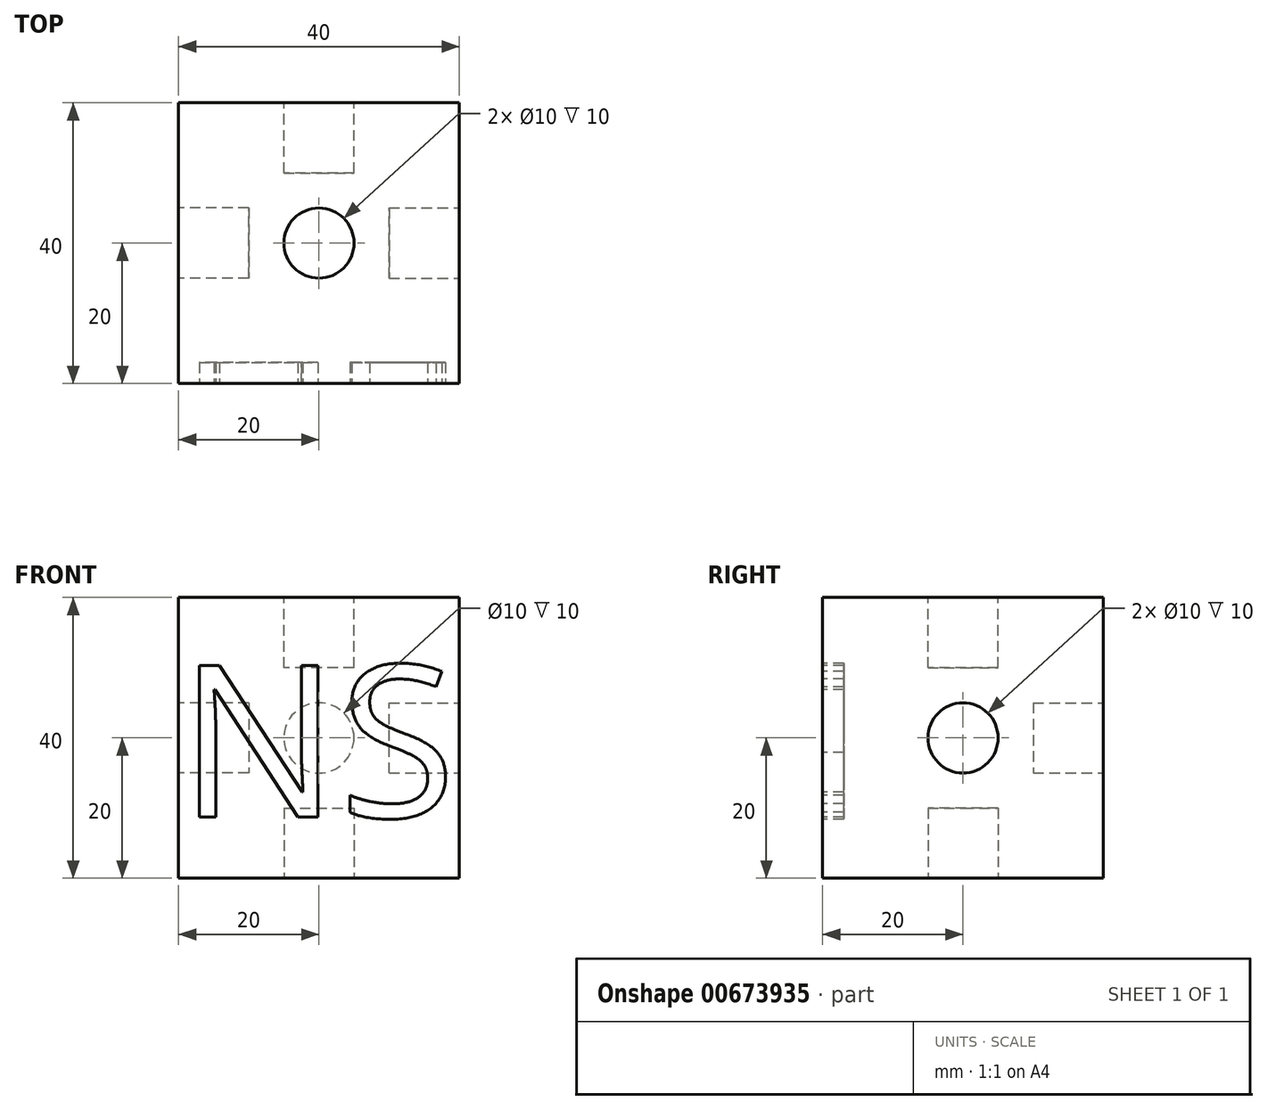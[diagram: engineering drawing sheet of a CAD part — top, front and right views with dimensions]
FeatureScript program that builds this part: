
annotation { "Feature Type Name" : "Feature", "Feature Type Description" : "" }
export const myFeature = defineFeature(function(context is Context, id is Id, definition is map)
    precondition{}
    {
        {
            var Q0;
            Q0=qCreatedBy(makeId("Front.planeOp"),FACE);
            var sketch = newSketch(context, id + "F0", { "sketchPlane" : qUnion([Q0])});
            skLineSegment(sketch, "E0.bottom", {"start": v(0, 0) * mm, "end": v(40, 0) * mm});
            skLineSegment(sketch, "E0.top", {"start": v(0, 40) * mm, "end": v(40, 40) * mm});
            skLineSegment(sketch, "E0.left", {"start": v(0, 0) * mm, "end": v(0, 40) * mm});
            skLineSegment(sketch, "E0.right", {"start": v(40, 0) * mm, "end": v(40, 40) * mm});
            skSolve(sketch);
        }
        {
            var Q0;
            Q0 = qSketchRegion(id + "F0", true);
            extrude(context, id + "F1", {"entities" : qUnion([Q0]), "depth" : 40 * mm, "offsetDistance" : 25 * mm});
        }
        {
            var Q0;
            Q0=makeQuery(id+"F1.opExtrude","SWEPT_FACE",FACE,{"disambiguationData":[OSD([sQuery(id+"F0.wireOp",EDGE,"E0.left")])]});
            var sketch = newSketch(context, id + "F2", { "sketchPlane" : qUnion([Q0])});
            skCircle(sketch, "E1", {"center": v(20, 20) * mm, "radius": 5 * mm});
            skPoint(sketch, "E1.centerSnap0", {"position": v(20, 40) * mm});
            skPoint(sketch, "E1.centerSnap1", {"position": v(0, 20) * mm});
            skSolve(sketch);
        }
        {
            var Q0;
            Q0 = qSketchRegion(id + "F2", true);
            extrude(context, id + "F3", {"entities" : qUnion([Q0]), "operationType" : NewBodyOperationType.REMOVE, "depth" : -10 * mm, "offsetDistance" : 25 * mm});
        }
        {
            var Q0;
            Q0=makeQuery(id+"F1.opExtrude","SWEPT_FACE",FACE,{"disambiguationData":[OSD([sQuery(id+"F0.wireOp",EDGE,"E0.right")])]});
            var sketch = newSketch(context, id + "F4", { "sketchPlane" : qUnion([Q0])});
            skCircle(sketch, "E2", {"center": v(-20, 20) * mm, "radius": 5 * mm});
            skPoint(sketch, "E2.centerSnap0", {"position": v(0, 20) * mm});
            skPoint(sketch, "E2.centerSnap1", {"position": v(-20, 0) * mm});
            skSolve(sketch);
        }
        {
            var Q0;
            Q0 = qSketchRegion(id + "F4", true);
            extrude(context, id + "F5", {"entities" : qUnion([Q0]), "operationType" : NewBodyOperationType.REMOVE, "depth" : -10 * mm, "offsetDistance" : 25 * mm});
        }
        {
            var Q0;
            Q0=makeQuery(id+"F1.opExtrude","CAP_FACE",FACE,{"disambiguationData":[OSD([sQuery(id+"F0.wireOp",EDGE,"E0.bottom"),sQuery(id+"F0.wireOp",EDGE,"E0.top"),sQuery(id+"F0.wireOp",EDGE,"E0.left"),sQuery(id+"F0.wireOp",EDGE,"E0.right")])],"isStart":false});
            var sketch = newSketch(context, id + "F6", { "sketchPlane" : qUnion([Q0])});
            skText(sketch, "E3", { "text": "NS", "fontName": "OpenSans-Regular.ttf"});
            const initialGuessF6  = {"E3": [0, 0.0087, 1, 0, 0.02182]};
            skSetInitialGuess(sketch, initialGuessF6);
            skSolve(sketch);
        }
        {
            var Q0;
            Q0 = qSketchRegion(id + "F6", true);
            extrude(context, id + "F7", {"entities" : qUnion([Q0]), "operationType" : NewBodyOperationType.REMOVE, "oppositeDirection" : true, "depth" : 3 * mm, "offsetDistance" : 25 * mm});
        }
        {
            var Q0;
            Q0=makeQuery(id+"F1.opExtrude","SWEPT_FACE",FACE,{"disambiguationData":[OSD([sQuery(id+"F0.wireOp",EDGE,"E0.top")])]});
            var sketch = newSketch(context, id + "F8", { "sketchPlane" : qUnion([Q0])});
            skCircle(sketch, "E4", {"center": v(20, -20) * mm, "radius": 5 * mm});
            skPoint(sketch, "E4.centerSnap0", {"position": v(20, 0) * mm});
            skPoint(sketch, "E4.centerSnap1", {"position": v(0, -20) * mm});
            skSolve(sketch);
        }
        {
            var Q0;
            Q0 = qSketchRegion(id + "F8", true);
            extrude(context, id + "F9", {"entities" : qUnion([Q0]), "operationType" : NewBodyOperationType.REMOVE, "oppositeDirection" : true, "depth" : 10 * mm, "offsetDistance" : 25 * mm});
        }
        {
            var Q0;
            Q0=makeQuery(id+"F1.opExtrude","SWEPT_FACE",FACE,{"disambiguationData":[OSD([sQuery(id+"F0.wireOp",EDGE,"E0.bottom")])]});
            var sketch = newSketch(context, id + "F10", { "sketchPlane" : qUnion([Q0])});
            skCircle(sketch, "E5", {"center": v(20, 20) * mm, "radius": 5 * mm});
            skPoint(sketch, "E5.centerSnap0", {"position": v(20, 40) * mm});
            skPoint(sketch, "E5.centerSnap1", {"position": v(0, 20) * mm});
            skSolve(sketch);
        }
        {
            var Q0;
            Q0 = qSketchRegion(id + "F10", true);
            extrude(context, id + "F11", {"entities" : qUnion([Q0]), "operationType" : NewBodyOperationType.REMOVE, "oppositeDirection" : true, "depth" : 10 * mm, "offsetDistance" : 25 * mm});
        }
        {
            var Q0;
            Q0=makeQuery(id+"F1.opExtrude","CAP_FACE",FACE,{"disambiguationData":[OSD([sQuery(id+"F0.wireOp",EDGE,"E0.bottom"),sQuery(id+"F0.wireOp",EDGE,"E0.top"),sQuery(id+"F0.wireOp",EDGE,"E0.left"),sQuery(id+"F0.wireOp",EDGE,"E0.right")])],"isStart":true});
            var sketch = newSketch(context, id + "F12", { "sketchPlane" : qUnion([Q0])});
            skCircle(sketch, "E6", {"center": v(-20, 20) * mm, "radius": 5 * mm});
            skPoint(sketch, "E6.centerSnap0", {"position": v(-20, 0) * mm});
            skPoint(sketch, "E6.centerSnap1", {"position": v(0, 20) * mm});
            skSolve(sketch);
        }
        {
            var Q0;
            Q0 = qSketchRegion(id + "F12", true);
            extrude(context, id + "F13", {"entities" : qUnion([Q0]), "operationType" : NewBodyOperationType.REMOVE, "oppositeDirection" : true, "depth" : 10 * mm, "offsetDistance" : 25 * mm});
        }
    });
